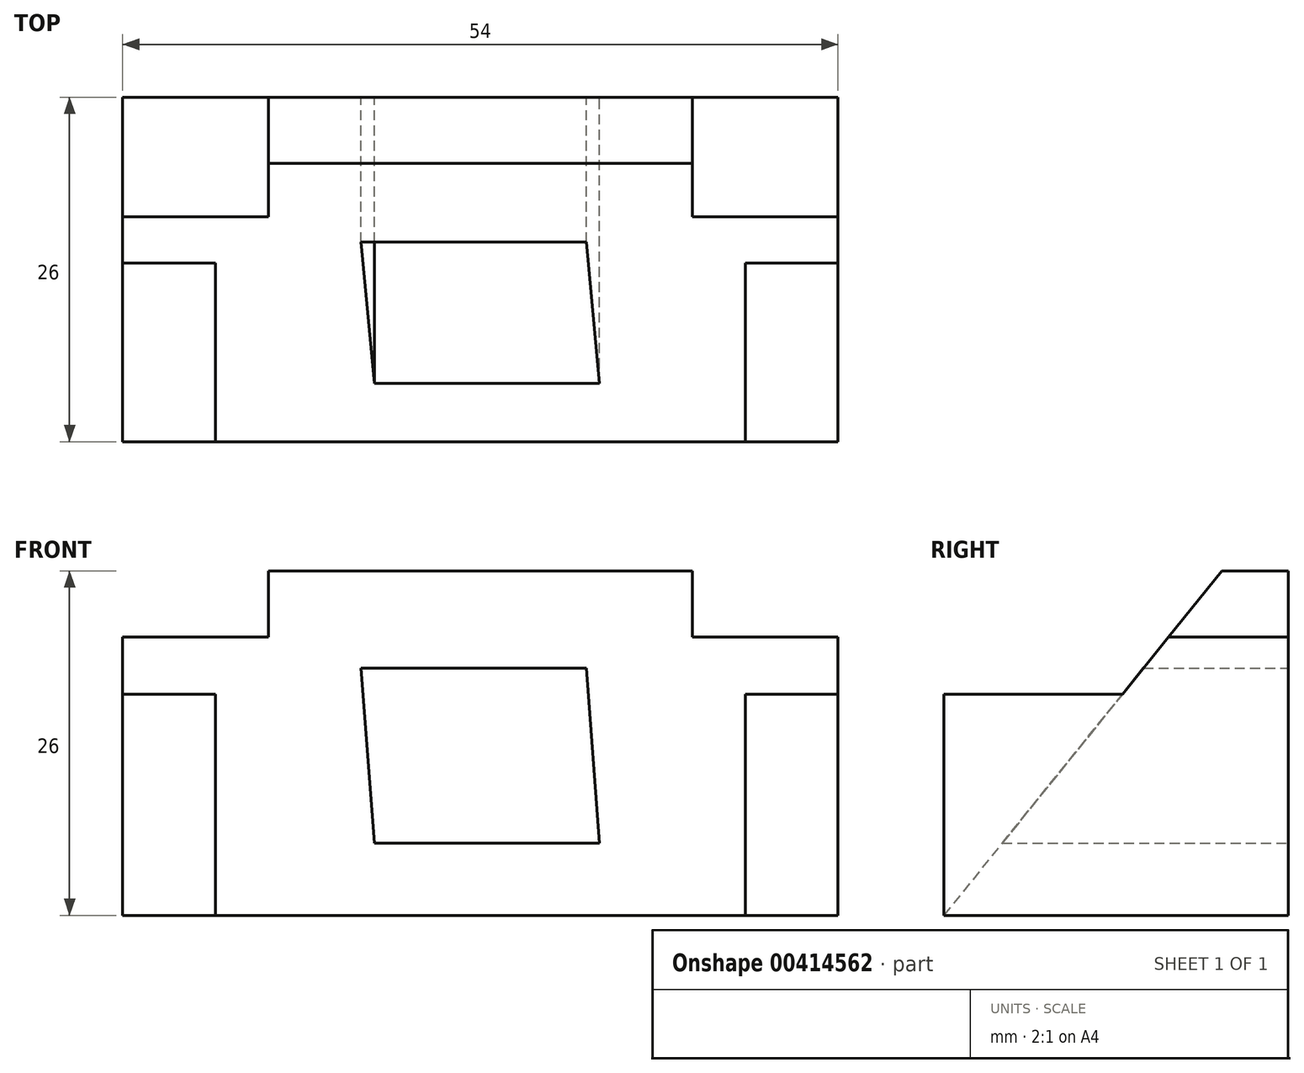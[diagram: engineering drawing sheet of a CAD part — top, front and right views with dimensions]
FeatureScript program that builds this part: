
annotation { "Feature Type Name" : "Feature", "Feature Type Description" : "" }
export const myFeature = defineFeature(function(context is Context, id is Id, definition is map)
    precondition{}
    {
        {
            var Q0;
            Q0=qCreatedBy(makeId("Front.planeOp"),FACE);
            var sketch = newSketch(context, id + "F0", { "sketchPlane" : qUnion([Q0])});
            skLineSegment(sketch, "E0.bottom", {"start": v(27, -13) * mm, "end": v(-27, -13) * mm});
            skLineSegment(sketch, "E0.top", {"start": v(27, 13) * mm, "end": v(-27, 13) * mm});
            skLineSegment(sketch, "E0.left", {"start": v(27, -13) * mm, "end": v(27, 13) * mm});
            skLineSegment(sketch, "E0.right", {"start": v(-27, -13) * mm, "end": v(-27, 13) * mm});
            skPoint(sketch, "E0.middle", {"position": v(0, 0) * mm});
            skSolve(sketch);
        }
        {
            var Q0;
            Q0 = qSketchRegion(id + "F0", true);
            extrude(context, id + "F1", {"entities" : qUnion([Q0]), "depth" : 26 * mm});
        }
        {
            var Q0;
            Q0=makeQuery(id+"F1.opExtrude","SWEPT_FACE",FACE,{"disambiguationData":[OSD([sQuery(id+"F0.wireOp",EDGE,"E0.left")])]});
            var sketch = newSketch(context, id + "F2", { "sketchPlane" : qUnion([Q0])});
            skLineSegment(sketch, "E1", {"start": v(0, 13) * mm, "end": v(-5, 13) * mm});
            skLineSegment(sketch, "E2", {"start": v(-5, 13) * mm, "end": v(-26, -13) * mm});
            skSolve(sketch);
        }
        {
            var Q0;
            {var subQ0=sQuery(id+"F2.wireOp",EDGE,"E2");Q0=makeQuery(id+"F2.imprint","IMPRINT",FACE,{"disambiguationData":[TD([[makeQuery(id+"F2.imprint","IMPRINT",EDGE,{"derivedFrom":subQ0}),-1.0]])]});}
            extrude(context, id + "F3", {"entities" : qUnion([Q0]), "operationType" : NewBodyOperationType.REMOVE, "oppositeDirection" : true, "depth" : 72.1 * mm});
        }
        {
            var Q0;
            Q0=makeQuery(id+"F1.opExtrude","CAP_FACE",FACE,{"disambiguationData":[OSD([sQuery(id+"F0.wireOp",EDGE,"E0.bottom"),sQuery(id+"F0.wireOp",EDGE,"E0.top"),sQuery(id+"F0.wireOp",EDGE,"E0.left"),sQuery(id+"F0.wireOp",EDGE,"E0.right")])],"isStart":true});
            var sketch = newSketch(context, id + "F4", { "sketchPlane" : qUnion([Q0])});
            skLineSegment(sketch, "E3", {"start": v(-27, -13) * mm, "end": v(-20, -13) * mm});
            skLineSegment(sketch, "E4", {"start": v(-27, -13) * mm, "end": v(-27, 3.7) * mm});
            skLineSegment(sketch, "E5", {"start": v(-27, 3.7) * mm, "end": v(-20, 3.7) * mm});
            skLineSegment(sketch, "E6", {"start": v(-20, 3.7) * mm, "end": v(-20, -13) * mm});
            skLineSegment(sketch, "E7", {"start": v(27, 3.7) * mm, "end": v(27, -13) * mm});
            skLineSegment(sketch, "E8", {"start": v(27, -13) * mm, "end": v(20, -13) * mm});
            skLineSegment(sketch, "E9", {"start": v(20, -13) * mm, "end": v(20, 3.7) * mm});
            skLineSegment(sketch, "E10", {"start": v(20, 3.7) * mm, "end": v(27, 3.7) * mm});
            skSolve(sketch);
        }
        {
            var Q0;
            Q0 = qSketchRegion(id + "F4", true);
            extrude(context, id + "F5", {"entities" : qUnion([Q0]), "operationType" : NewBodyOperationType.ADD, "oppositeDirection" : true, "depth" : 26 * mm});
        }
        {
            var Q0;
            Q0=makeQuery(id+"F1.opExtrude","CAP_FACE",FACE,{"disambiguationData":[OSD([sQuery(id+"F0.wireOp",EDGE,"E0.bottom"),sQuery(id+"F0.wireOp",EDGE,"E0.top"),sQuery(id+"F0.wireOp",EDGE,"E0.left"),sQuery(id+"F0.wireOp",EDGE,"E0.right")])],"isStart":true});
            var sketch = newSketch(context, id + "F6", { "sketchPlane" : qUnion([Q0])});
            skLineSegment(sketch, "E11", {"start": v(-27, 13) * mm, "end": v(-27, 8) * mm});
            skLineSegment(sketch, "E12", {"start": v(-27, 8) * mm, "end": v(-27, 13) * mm});
            skLineSegment(sketch, "E13", {"start": v(-27, 13) * mm, "end": v(-16, 13) * mm});
            skLineSegment(sketch, "E14", {"start": v(-16, 13) * mm, "end": v(-16, 8) * mm});
            skLineSegment(sketch, "E15", {"start": v(-16, 8) * mm, "end": v(-27, 8) * mm});
            skLineSegment(sketch, "E16", {"start": v(27, 13) * mm, "end": v(27, 8) * mm});
            skLineSegment(sketch, "E17", {"start": v(27, 8) * mm, "end": v(16, 8) * mm});
            skLineSegment(sketch, "E18", {"start": v(27, 13) * mm, "end": v(16, 13) * mm});
            skLineSegment(sketch, "E19", {"start": v(16, 13) * mm, "end": v(16, 8) * mm});
            skSolve(sketch);
        }
        {
            var Q0;
            Q0 = qSketchRegion(id + "F6", true);
            extrude(context, id + "F7", {"entities" : qUnion([Q0]), "operationType" : NewBodyOperationType.REMOVE, "oppositeDirection" : true, "depth" : 25 * mm});
        }
        {
            var Q0;
            Q0=makeQuery(id+"F3.boolean.opBoolean","COPY",FACE,{"derivedFrom":makeQuery(id+"F3.opExtrude","SWEPT_FACE",FACE,{"disambiguationData":[OSD([sQuery(id+"F2.wireOp",EDGE,"E2")])]})});
            var sketch = newSketch(context, id + "F8", { "sketchPlane" : qUnion([Q0])});
            skLineSegment(sketch, "E20", {"start": v(-20, -26.45) * mm, "end": v(-9, -26.45) * mm});
            skLineSegment(sketch, "E21", {"start": v(20, -26.45) * mm, "end": v(9, -26.45) * mm});
            skLineSegment(sketch, "E22", {"start": v(9, -26.45) * mm, "end": v(9, -19.45) * mm});
            skLineSegment(sketch, "E23", {"start": v(-9, -26.45) * mm, "end": v(-9, -19.45) * mm});
            skLineSegment(sketch, "E24", {"start": v(9, -19.45) * mm, "end": v(-8, -19.45) * mm});
            skLineSegment(sketch, "E25", {"start": v(-8, -19.45) * mm, "end": v(-9, -2.48) * mm});
            skLineSegment(sketch, "E26", {"start": v(-9, -2.48) * mm, "end": v(8, -2.48) * mm});
            skLineSegment(sketch, "E27", {"start": v(8, -2.48) * mm, "end": v(9, -19.45) * mm});
            skLineSegment(sketch, "E28", {"start": v(8, -2.48) * mm, "end": v(-9, -2.48) * mm});
            skSolve(sketch);
        }
        {
            var Q0;
            Q0=makeQuery(id+"F1.opExtrude","CAP_FACE",FACE,{"disambiguationData":[OSD([sQuery(id+"F0.wireOp",EDGE,"E0.bottom"),sQuery(id+"F0.wireOp",EDGE,"E0.top"),sQuery(id+"F0.wireOp",EDGE,"E0.left"),sQuery(id+"F0.wireOp",EDGE,"E0.right")])],"isStart":true});
            var sketch = newSketch(context, id + "F9", { "sketchPlane" : qUnion([Q0])});
            skPoint(sketch, "E29.0", {"position": v(0.5, 5.65) * mm});
            skLineSegment(sketch, "E30.0", {"start": v(-8, 5.65) * mm, "end": v(9, 5.65) * mm});
            skPoint(sketch, "E31.0", {"position": v(9, 5.65) * mm});
            skPoint(sketch, "E32.0", {"position": v(8, -7.55) * mm});
            skLineSegment(sketch, "E33.0", {"start": v(8, -7.55) * mm, "end": v(9, 5.65) * mm});
            skLineSegment(sketch, "E34.0.0", {"start": v(9, -13) * mm, "end": v(-9, -13) * mm});
            skLineSegment(sketch, "E34.0.1", {"start": v(-9, -13) * mm, "end": v(-20, -13) * mm});
            skLineSegment(sketch, "E34.0.2", {"start": v(-20, -13) * mm, "end": v(-20, 3.7) * mm});
            skLineSegment(sketch, "E34.0.3", {"start": v(-20, 3.7) * mm, "end": v(-27, 3.7) * mm});
            skLineSegment(sketch, "E34.0.4", {"start": v(-27, 3.7) * mm, "end": v(-27, 8) * mm});
            skLineSegment(sketch, "E34.0.5", {"start": v(-27, 8) * mm, "end": v(-16, 8) * mm});
            skLineSegment(sketch, "E34.0.6", {"start": v(-16, 8) * mm, "end": v(-16, 13) * mm});
            skLineSegment(sketch, "E34.0.7", {"start": v(-16, 13) * mm, "end": v(16, 13) * mm});
            skLineSegment(sketch, "E34.0.8", {"start": v(16, 13) * mm, "end": v(16, 8) * mm});
            skLineSegment(sketch, "E34.0.9", {"start": v(16, 8) * mm, "end": v(27, 8) * mm});
            skLineSegment(sketch, "E34.0.10", {"start": v(27, 8) * mm, "end": v(27, 3.7) * mm});
            skLineSegment(sketch, "E34.0.11", {"start": v(27, 3.7) * mm, "end": v(20, 3.7) * mm});
            skLineSegment(sketch, "E34.0.12", {"start": v(20, 3.7) * mm, "end": v(20, -13) * mm});
            skLineSegment(sketch, "E34.0.13", {"start": v(20, -13) * mm, "end": v(9, -13) * mm});
            skPoint(sketch, "E35.0", {"position": v(-9, -7.55) * mm});
            skLineSegment(sketch, "E36.0", {"start": v(-8, 5.65) * mm, "end": v(-9, -7.55) * mm});
            skLineSegment(sketch, "E37.0", {"start": v(-9, -7.55) * mm, "end": v(8, -7.55) * mm});
            skSolve(sketch);
        }
        {
            var Q1;
            Q1=makeQuery(id+"F8.imprint","IMPRINT",FACE,{"disambiguationData":[TD([[makeQuery(id+"F8.imprint","IMPRINT",EDGE,{"derivedFrom":sQuery(id+"F8.wireOp",EDGE,"E24")}),-1.0]])]});
            var Q2;
            Q2=makeQuery(id+"F9.imprint","IMPRINT",FACE,{"disambiguationData":[TD([[makeQuery(id+"F9.imprint","IMPRINT",EDGE,{"derivedFrom":sQuery(id+"F9.wireOp",EDGE,"E30.0")}),-1.0]])]});
            loft(context, id + "F10", {"operationType" : NewBodyOperationType.REMOVE, "sheetProfilesArray" : [{ "sheetProfileEntities" : qUnion([Q1]) }, { "sheetProfileEntities" : qUnion([Q2]) }]});
        }
    });
